# Revit family: Sanitary-Taps&Mixers_E.C.A._Luna-Basin-Mixer_102108940EX
name_source: partatom
category: Generic Models
revit_build: Autodesk Revit 2015 (Build: 20140606_1530(x64)
units: mm (PartAtom-declared; Revit-internal decimal feet)

## types (1)
- Luna Lavabo
    Accessories = www.eca.com.tr
    Asset Type = Fixed
    BIMObject Name = E.C.A. Luna Basin Mixer
    BIMobject category = Taps & Mixers
    BIMobject category code = sanitary-taps-mixers
    BIMobject main category = Sanitary
    BIMobject main category code = sanitary
    Brand = E.C.A.
    Brand url = https://www.eca.com.tr
    CW Connection = Yes
    Color = Chrome
    Connection = G 3/8''
    Connection Type = Plumbing
    Cost = 0 $
    Default Elevation = 0 mm  [stored 0 ft]
    Depth = 171 mm
    Design country = Turkey
    Edition number = 1
    Faucet Material = Brass
    HW Connection = Yes
    Height = 187 mm
    Hygiene Plus = No
    IFC Classification = Sanitary Terminal
    Installation instructions = http://www.eca.com.tr
    LEED Credit = Yes
    Low Emiting Material / Green Guard Gold = Yes
    Manufacturer = Valfsel Armatür Sanayi A.Ş.
    Manufacturer URL = www.valfsel.com.tr
    Manufacturer country = Turkey
    Manufacturer name = E.C.A.
    Masterformat 2014 Code = 22 41 39
    Masterformat 2014 Description = Residential Faucets, Supplies, and Trim
    Material Main = Chrome
    Model = E.C.A. Luna
    NBS Reference Code = 31-75
    NBS Reference Description = Sanitary Accessories
    Nominal height = 187 mm
    Nominal width = 50 mm
    OmniClass Code = 23-31 11 00
    OmniClass Description = Faucets
    Outlet Height = 121 mm
    Outlet Lenght = 132 mm
    Product Code = 102108940
    Product Export Code (Localization product codes are available) = 102108940 EX
    Product Family = E.C.A. Luna
    Product Group = Basin Mixer
    Product Guid = c65992ff-ea75-45db-9f55-701278c7bf98
    Product SKU = 102108940EX
    Product certification = http://www.eca.com.tr
    Product data url = https://bimobject.com
    Product url = http://www.eca.com.tr
    QR code = http://bimobject.com
    Space = Internal
    Technical description = http://www.eca.com.tr
    Test Pressure = 10 Bar
    UNSPSC Code = 301815
    URL = www.eca.com.tr
    Uniclass 1.4 Code = L725111
    Uniclass 1.4 Description = Mixer taps
    Uniclass 2.0 Code = PR-31-75
    Uniclass 2.0 Description = Sanitary Accessories
    Uniclass 2015 Code = Pr_40_20_87_98
    Uniclass 2015 Name = Washbasin taps
    Uniformat II Code = D2010
    Uniformat II Description = Plumbing Fixtures
    Valve Operation = Lever
    Vent Connection = No
    Volume Units = Litres
    Warranty Description = Manufacturer Warranty
    Waste Connection = No
    Water Efficient Product = Yes
    Water Label = Yes
    Weight Net (Kg) = 1.4
    Width = 50 mm
    Working Pressure = 0,1 - 3 Bar

note: [stored X ft] marks values corroborated as IEEE doubles in the binary element streams (Revit-internal decimal feet)

## geometry (parser evidence)
native form markers: Blend x4
no freeform markers — native parametric forms only
